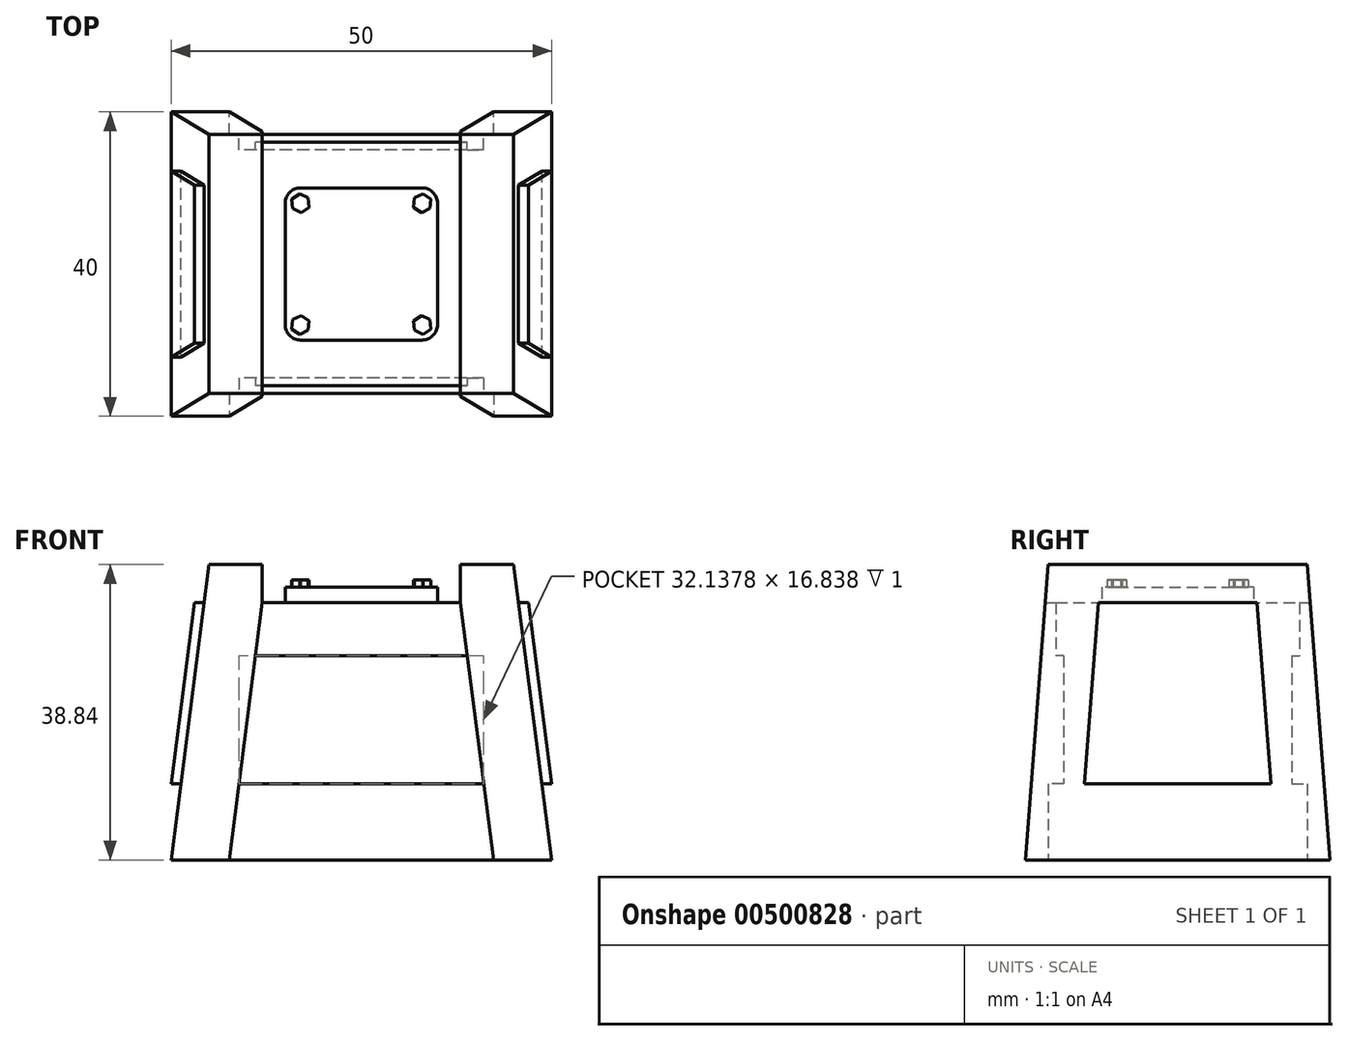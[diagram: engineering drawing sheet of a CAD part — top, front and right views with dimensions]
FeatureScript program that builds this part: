
annotation { "Feature Type Name" : "Feature", "Feature Type Description" : "" }
export const myFeature = defineFeature(function(context is Context, id is Id, definition is map)
    precondition{}
    {
        {
            var Q0;
            Q0=qCreatedBy(makeId("Front.planeOp"),FACE);
            var sketch = newSketch(context, id + "F0", { "sketchPlane" : qUnion([Q0])});
            skLineSegment(sketch, "E0", {"start": v(-25, 0) * mm, "end": v(25, 0) * mm});
            skPoint(sketch, "E1", {"position": v(0, 0) * mm});
            skLineSegment(sketch, "E2", {"start": v(-25, 0) * mm, "end": v(-20, 38.84) * mm});
            skLineSegment(sketch, "E3", {"start": v(-13, 38.84) * mm, "end": v(-13, 33.84) * mm});
            skLineSegment(sketch, "E4", {"start": v(-13, 33.84) * mm, "end": v(0, 33.84) * mm});
            skLineSegment(sketch, "E5", {"start": v(-13, 33.84) * mm, "end": v(-17.36, 0) * mm});
            skLineSegment(sketch, "E6", {"start": v(0, 10) * mm, "end": v(-16.07, 10) * mm});
            skLineSegment(sketch, "E7", {"start": v(0, 26.84) * mm, "end": v(-13.9, 26.84) * mm});
            skLineSegment(sketch, "E8", {"start": v(0, 0) * mm, "end": v(0, 10) * mm, "construction": true});
            skLineSegment(sketch, "E9", {"start": v(0, 0) * mm, "end": v(0, 38.84) * mm, "construction": true});
            skLineSegment(sketch, "E10", {"start": v(0, 38.84) * mm, "end": v(0, 33.84) * mm, "construction": true});
            skLineSegment(sketch, "E11", {"start": v(0, 33.84) * mm, "end": v(0, 26.84) * mm, "construction": true});
            skLineSegment(sketch, "E12", {"start": v(-20, 38.84) * mm, "end": v(-13, 38.84) * mm});
            skLineSegment(sketch, "E13.MirrorCS", {"start": v(0, 10) * mm, "end": v(16.07, 10) * mm});
            skLineSegment(sketch, "E14.MirrorCS", {"start": v(13, 33.84) * mm, "end": v(17.36, 0) * mm});
            skLineSegment(sketch, "E15.MirrorCS", {"start": v(0, 26.84) * mm, "end": v(13.9, 26.84) * mm});
            skLineSegment(sketch, "E16.MirrorCS", {"start": v(13, 33.84) * mm, "end": v(0, 33.84) * mm});
            skLineSegment(sketch, "E17.MirrorCS", {"start": v(13, 38.84) * mm, "end": v(13, 33.84) * mm});
            skLineSegment(sketch, "E18.MirrorCS", {"start": v(25, 0) * mm, "end": v(20, 38.84) * mm});
            skLineSegment(sketch, "E19.MirrorCS", {"start": v(20, 38.84) * mm, "end": v(13, 38.84) * mm});
            skLineSegment(sketch, "E20", {"start": v(0, 38.84) * mm, "end": v(-20, 38.84) * mm, "construction": true});
            skLineSegment(sketch, "E21", {"start": v(-25, 0) * mm, "end": v(-25, 38.84) * mm});
            skLineSegment(sketch, "E22", {"start": v(-25, 38.84) * mm, "end": v(-20, 38.84) * mm});
            skLineSegment(sketch, "E23.MirrorCS", {"start": v(25, 0) * mm, "end": v(25, 38.84) * mm});
            skLineSegment(sketch, "E24.MirrorCS", {"start": v(25, 38.84) * mm, "end": v(20, 38.84) * mm});
            skLineSegment(sketch, "E25", {"start": v(16.07, 10) * mm, "end": v(25, 10) * mm, "construction": true});
            skLineSegment(sketch, "E26", {"start": v(25, 10) * mm, "end": v(21.29, 38.84) * mm});
            skLineSegment(sketch, "E27.MirrorCS", {"start": v(-25, 10) * mm, "end": v(-21.29, 38.84) * mm});
            skSolve(sketch);
        }
        {
            var Q0;
            {var subQ3=sQuery(id+"F0.wireOp",EDGE,"E2");Q0=makeQuery(id+"F0.imprint","IMPRINT",FACE,{"disambiguationData":[TD([[makeQuery(id+"F0.imprint","IMPRINT",EDGE,{"derivedFrom":subQ3}),-1.0]])]});}
            var Q1;
            {var subQ6=sQuery(id+"F0.wireOp",EDGE,"E6");Q1=makeQuery(id+"F0.imprint","IMPRINT",FACE,{"disambiguationData":[TD([[makeQuery(id+"F0.imprint","IMPRINT",EDGE,{"derivedFrom":subQ6}),1.0]])]});}
            var Q2;
            {var subQ1=sQuery(id+"F0.wireOp",EDGE,"E6");Q2=makeQuery(id+"F0.imprint","IMPRINT",FACE,{"disambiguationData":[TD([[makeQuery(id+"F0.imprint","IMPRINT",EDGE,{"derivedFrom":subQ1}),-1.0]])]});}
            var Q3;
            {var subQ4=sQuery(id+"F0.wireOp",EDGE,"E4");Q3=makeQuery(id+"F0.imprint","IMPRINT",FACE,{"disambiguationData":[TD([[makeQuery(id+"F0.imprint","IMPRINT",EDGE,{"derivedFrom":subQ4}),-1.0]])]});}
            var Q4;
            {var subQ5=sQuery(id+"F0.wireOp",EDGE,"E17.MirrorCS");Q4=makeQuery(id+"F0.imprint","IMPRINT",FACE,{"disambiguationData":[TD([[makeQuery(id+"F0.imprint","IMPRINT",EDGE,{"derivedFrom":subQ5}),1.0]])]});}
            extrude(context, id + "F1", {"entities" : qUnion([Q0, Q1, Q2, Q3, Q4]), "depth" : 40 * mm});
        }
        {
            var Q0;
            {var subQ4=sQuery(id+"F0.wireOp",EDGE,"E4");Q0=makeQuery(id+"F0.imprint","IMPRINT",FACE,{"disambiguationData":[TD([[makeQuery(id+"F0.imprint","IMPRINT",EDGE,{"derivedFrom":subQ4}),-1.0]])]});}
            extrude(context, id + "F2", {"entities" : qUnion([Q0]), "operationType" : NewBodyOperationType.REMOVE, "depth" : 4 * mm});
        }
        {
            var Q0;
            {var subQ6=sQuery(id+"F0.wireOp",EDGE,"E6");Q0=makeQuery(id+"F0.imprint","IMPRINT",FACE,{"disambiguationData":[TD([[makeQuery(id+"F0.imprint","IMPRINT",EDGE,{"derivedFrom":subQ6}),1.0]])]});}
            extrude(context, id + "F3", {"entities" : qUnion([Q0]), "operationType" : NewBodyOperationType.REMOVE, "depth" : 3 * mm});
        }
        {
            var Q0;
            {var subQ1=sQuery(id+"F0.wireOp",EDGE,"E6");Q0=makeQuery(id+"F0.imprint","IMPRINT",FACE,{"disambiguationData":[TD([[makeQuery(id+"F0.imprint","IMPRINT",EDGE,{"derivedFrom":subQ1}),-1.0]])]});}
            extrude(context, id + "F4", {"entities" : qUnion([Q0]), "operationType" : NewBodyOperationType.REMOVE, "depth" : 5 * mm});
        }
        {
            var Q0;
            Q0=makeQuery(id+"F1.opExtrude","CAP_FACE",FACE,{"disambiguationData":[OSD([sQuery(id+"F0.wireOp",EDGE,"E0"),sQuery(id+"F0.wireOp",EDGE,"E2"),sQuery(id+"F0.wireOp",EDGE,"E3"),sQuery(id+"F0.wireOp",EDGE,"E4"),sQuery(id+"F0.wireOp",EDGE,"E12"),sQuery(id+"F0.wireOp",EDGE,"E16.MirrorCS"),sQuery(id+"F0.wireOp",EDGE,"E17.MirrorCS"),sQuery(id+"F0.wireOp",EDGE,"E18.MirrorCS"),sQuery(id+"F0.wireOp",EDGE,"E19.MirrorCS")])],"isStart":false});
            var sketch = newSketch(context, id + "F5", { "sketchPlane" : qUnion([Q0])});
            skLineSegment(sketch, "E28", {"start": v(-25, 0) * mm, "end": v(25, 0) * mm});
            skPoint(sketch, "E29", {"position": v(0, 0) * mm});
            skLineSegment(sketch, "E30", {"start": v(-25, 0) * mm, "end": v(-20, 38.84) * mm});
            skLineSegment(sketch, "E31", {"start": v(-13, 38.84) * mm, "end": v(-13, 33.84) * mm});
            skLineSegment(sketch, "E32", {"start": v(-13, 33.84) * mm, "end": v(0, 33.84) * mm});
            skLineSegment(sketch, "E33", {"start": v(-13, 33.84) * mm, "end": v(-17.36, 0) * mm});
            skLineSegment(sketch, "E34", {"start": v(0, 10) * mm, "end": v(-16.07, 10) * mm});
            skLineSegment(sketch, "E35", {"start": v(0, 26.84) * mm, "end": v(-13.9, 26.84) * mm});
            skLineSegment(sketch, "E36", {"start": v(0, 0) * mm, "end": v(0, 10) * mm, "construction": true});
            skLineSegment(sketch, "E37", {"start": v(0, 0) * mm, "end": v(0, 38.84) * mm, "construction": true});
            skLineSegment(sketch, "E38", {"start": v(0, 38.84) * mm, "end": v(0, 33.84) * mm, "construction": true});
            skLineSegment(sketch, "E39", {"start": v(0, 33.84) * mm, "end": v(0, 26.84) * mm, "construction": true});
            skLineSegment(sketch, "E40", {"start": v(-20, 38.84) * mm, "end": v(-13, 38.84) * mm});
            skLineSegment(sketch, "E41.MirrorCS", {"start": v(0, 10) * mm, "end": v(16.07, 10) * mm});
            skLineSegment(sketch, "E42.MirrorCS", {"start": v(13, 33.84) * mm, "end": v(17.36, 0) * mm});
            skLineSegment(sketch, "E43.MirrorCS", {"start": v(0, 26.84) * mm, "end": v(13.9, 26.84) * mm});
            skLineSegment(sketch, "E44.MirrorCS", {"start": v(13, 33.84) * mm, "end": v(0, 33.84) * mm});
            skLineSegment(sketch, "E45.MirrorCS", {"start": v(13, 38.84) * mm, "end": v(13, 33.84) * mm});
            skLineSegment(sketch, "E46.MirrorCS", {"start": v(25, 0) * mm, "end": v(20, 38.84) * mm});
            skLineSegment(sketch, "E47.MirrorCS", {"start": v(20, 38.84) * mm, "end": v(13, 38.84) * mm});
            skLineSegment(sketch, "E48", {"start": v(0, 38.84) * mm, "end": v(-20, 38.84) * mm, "construction": true});
            skSolve(sketch);
        }
        {
            var Q0;
            {var subQ4=sQuery(id+"F5.wireOp",EDGE,"E32");Q0=makeQuery(id+"F5.imprint","IMPRINT",FACE,{"disambiguationData":[TD([[makeQuery(id+"F5.imprint","IMPRINT",EDGE,{"derivedFrom":subQ4}),-1.0]])]});}
            extrude(context, id + "F6", {"entities" : qUnion([Q0]), "operationType" : NewBodyOperationType.REMOVE, "oppositeDirection" : true, "depth" : 4 * mm});
        }
        {
            var Q0;
            {var subQ6=sQuery(id+"F5.wireOp",EDGE,"E34");Q0=makeQuery(id+"F5.imprint","IMPRINT",FACE,{"disambiguationData":[TD([[makeQuery(id+"F5.imprint","IMPRINT",EDGE,{"derivedFrom":subQ6}),1.0]])]});}
            extrude(context, id + "F7", {"entities" : qUnion([Q0]), "operationType" : NewBodyOperationType.REMOVE, "oppositeDirection" : true, "depth" : 3 * mm});
        }
        {
            var Q0;
            {var subQ1=sQuery(id+"F5.wireOp",EDGE,"E34");Q0=makeQuery(id+"F5.imprint","IMPRINT",FACE,{"disambiguationData":[TD([[makeQuery(id+"F5.imprint","IMPRINT",EDGE,{"derivedFrom":subQ1}),-1.0]])]});}
            extrude(context, id + "F8", {"entities" : qUnion([Q0]), "operationType" : NewBodyOperationType.REMOVE, "oppositeDirection" : true, "depth" : 5 * mm});
        }
        {
            var Q0;
            Q0=makeQuery(id+"F1.opExtrude","SWEPT_FACE",FACE,{"disambiguationData":[OSD([sQuery(id+"F0.wireOp",EDGE,"E4"),sQuery(id+"F0.wireOp",EDGE,"E16.MirrorCS")])]});
            var sketch = newSketch(context, id + "F9", { "sketchPlane" : qUnion([Q0])});
            skLineSegment(sketch, "E49", {"start": v(0, -4) * mm, "end": v(0, -36) * mm, "construction": true});
            skLineSegment(sketch, "E50", {"start": v(0, -20) * mm, "end": v(-13, -20) * mm, "construction": true});
            skLineSegment(sketch, "E51.bottom", {"start": v(-8, -30) * mm, "end": v(8, -30) * mm});
            skLineSegment(sketch, "E51.top", {"start": v(-8, -10) * mm, "end": v(8, -10) * mm});
            skLineSegment(sketch, "E51.left", {"start": v(-10, -28) * mm, "end": v(-10, -12) * mm});
            skLineSegment(sketch, "E51.right", {"start": v(10, -28) * mm, "end": v(10, -12) * mm});
            skLineSegment(sketch, "E52", {"start": v(0, -10) * mm, "end": v(0, -30) * mm, "construction": true});
            skLineSegment(sketch, "E53", {"start": v(-10, -20) * mm, "end": v(10, -20) * mm, "construction": true});
            skPoint(sketch, "E54", {"position": v(0, -20) * mm});
            skPoint(sketch, "E55.visualSharp", {"position": v(-10, -30) * mm});
            skArc(sketch, "E55.filletArc", {"start": v(-10, -28) * mm, "mid": v(-9.41, -29.41) * mm, "end": v(-8, -30) * mm});
            skPoint(sketch, "E56.visualSharp", {"position": v(-10, -10) * mm});
            skArc(sketch, "E56.filletArc", {"start": v(-8, -10) * mm, "mid": v(-9.41, -10.59) * mm, "end": v(-10, -12) * mm});
            skPoint(sketch, "E57.visualSharp", {"position": v(10, -10) * mm});
            skArc(sketch, "E57.filletArc", {"start": v(10, -12) * mm, "mid": v(9.41, -10.59) * mm, "end": v(8, -10) * mm});
            skPoint(sketch, "E58.visualSharp", {"position": v(10, -30) * mm});
            skArc(sketch, "E58.filletArc", {"start": v(8, -30) * mm, "mid": v(9.41, -29.41) * mm, "end": v(10, -28) * mm});
            skSolve(sketch);
        }
        {
            var Q0;
            Q0=makeQuery(id+"F9.imprint","IMPRINT",FACE,{"disambiguationData":[TD([[makeQuery(id+"F9.imprint","IMPRINT",EDGE,{"derivedFrom":sQuery(id+"F9.wireOp",EDGE,"E51.bottom")}),1.0]])]});
            extrude(context, id + "F10", {"entities" : qUnion([Q0]), "operationType" : NewBodyOperationType.ADD, "depth" : 2 * mm});
        }
        {
            var Q0;
            Q0=makeQuery(id+"F0.imprint","IMPRINT",FACE,{"disambiguationData":[TD([[makeQuery(id+"F0.imprint","IMPRINT",EDGE,{"derivedFrom":sQuery(id+"F0.wireOp",EDGE,"E2")}),1.0]])]});
            var Q1;
            Q1=sQuery(id+"F0.wireOp",EDGE,"E21");
            extrude(context, id + "F11", {"entities" : qUnion([Q0]), "bodyType" : ToolBodyType.SURFACE, "surfaceEntities" : qUnion([Q1]), "depth" : 40 * mm});
        }
        {
            var Q0;
            Q0=makeQuery(id+"F11.opExtrude","SWEPT_FACE",FACE,{"disambiguationData":[OSD([sQuery(id+"F0.wireOp",EDGE,"E21")])]});
            var sketch = newSketch(context, id + "F12", { "sketchPlane" : qUnion([Q0])});
            skLineSegment(sketch, "E59", {"start": v(0, 0) * mm, "end": v(-3, 38.84) * mm});
            skLineSegment(sketch, "E60", {"start": v(-3, 38.84) * mm, "end": v(0, 38.84) * mm, "construction": true});
            skLineSegment(sketch, "E61", {"start": v(-20, 0) * mm, "end": v(-20, 38.84) * mm, "construction": true});
            skLineSegment(sketch, "E62.MirrorCS", {"start": v(-40, 0) * mm, "end": v(-37, 38.84) * mm});
            skLineSegment(sketch, "E63", {"start": v(-40, 0) * mm, "end": v(-40, 10) * mm, "construction": true});
            skLineSegment(sketch, "E64", {"start": v(-40, 38.84) * mm, "end": v(-40, 33.84) * mm, "construction": true});
            skLineSegment(sketch, "E65", {"start": v(-37.39, 33.84) * mm, "end": v(-30.39, 33.84) * mm, "construction": true});
            skLineSegment(sketch, "E66", {"start": v(-30.39, 33.84) * mm, "end": v(-32.23, 10) * mm});
            skLineSegment(sketch, "E67", {"start": v(-32.23, 10) * mm, "end": v(-20, 10) * mm});
            skLineSegment(sketch, "E68", {"start": v(-30.39, 33.84) * mm, "end": v(-20, 33.84) * mm});
            skLineSegment(sketch, "E69.MirrorCS", {"start": v(-9.61, 33.84) * mm, "end": v(-20, 33.84) * mm});
            skLineSegment(sketch, "E70.MirrorCS", {"start": v(-9.61, 33.84) * mm, "end": v(-7.77, 10) * mm});
            skLineSegment(sketch, "E71.MirrorCS", {"start": v(-7.77, 10) * mm, "end": v(-20, 10) * mm});
            skSolve(sketch);
        }
        {
            var Q0;
            {var subQ0=sQuery(id+"F12.wireOp",EDGE,"E59");Q0=makeQuery(id+"F12.imprint","IMPRINT",FACE,{"disambiguationData":[TD([[makeQuery(id+"F12.imprint","IMPRINT",EDGE,{"derivedFrom":subQ0}),-1.0]])]});}
            var Q1;
            {var subQ0=sQuery(id+"F12.wireOp",EDGE,"E62.MirrorCS");Q1=makeQuery(id+"F12.imprint","IMPRINT",FACE,{"disambiguationData":[TD([[makeQuery(id+"F12.imprint","IMPRINT",EDGE,{"derivedFrom":subQ0}),1.0]])]});}
            extrude(context, id + "F13", {"entities" : qUnion([Q0, Q1]), "operationType" : NewBodyOperationType.REMOVE, "depth" : 50 * mm});
        }
        {
            var Q0;
            Q0=makeQuery(id+"F10.opExtrude","CAP_FACE",FACE,{"disambiguationData":[OSD([sQuery(id+"F9.wireOp",EDGE,"E51.bottom"),sQuery(id+"F9.wireOp",EDGE,"E51.top"),sQuery(id+"F9.wireOp",EDGE,"E51.left"),sQuery(id+"F9.wireOp",EDGE,"E51.right"),sQuery(id+"F9.wireOp",EDGE,"E55.filletArc"),sQuery(id+"F9.wireOp",EDGE,"E56.filletArc"),sQuery(id+"F9.wireOp",EDGE,"E57.filletArc"),sQuery(id+"F9.wireOp",EDGE,"E58.filletArc")])],"isStart":false});
            var sketch = newSketch(context, id + "F14", { "sketchPlane" : qUnion([Q0])});
            skLineSegment(sketch, "E72", {"start": v(-10, -12) * mm, "end": v(-8, -12) * mm, "construction": true});
            skLineSegment(sketch, "E73", {"start": v(-8, -12) * mm, "end": v(-8, -10) * mm, "construction": true});
            skCircle(sketch, "E74.cCircle", {"center": v(-8, -12) * mm, "radius": 1.25 * mm, "construction": true});
            skLineSegment(sketch, "E74.0", {"start": v(-6.87, -12.54) * mm, "end": v(-7.9, -13.25) * mm});
            skLineSegment(sketch, "E74.1", {"start": v(-7.9, -13.25) * mm, "end": v(-9.03, -12.7) * mm});
            skLineSegment(sketch, "E74.2", {"start": v(-9.03, -12.7) * mm, "end": v(-9.13, -11.46) * mm});
            skLineSegment(sketch, "E74.3", {"start": v(-9.13, -11.46) * mm, "end": v(-8.1, -10.75) * mm});
            skLineSegment(sketch, "E74.4", {"start": v(-8.1, -10.75) * mm, "end": v(-6.97, -11.3) * mm});
            skLineSegment(sketch, "E74.5", {"start": v(-6.97, -11.3) * mm, "end": v(-6.87, -12.54) * mm});
            skLineSegment(sketch, "E75", {"start": v(0, -10) * mm, "end": v(0, -30) * mm, "construction": true});
            skLineSegment(sketch, "E76", {"start": v(-10, -20) * mm, "end": v(10, -20) * mm, "construction": true});
            skCircle(sketch, "E77.MirrorC", {"center": v(-8, -28) * mm, "radius": 1.25 * mm, "construction": true});
            skLineSegment(sketch, "E78.MirrorCS", {"start": v(-6.87, -27.46) * mm, "end": v(-7.9, -26.75) * mm});
            skLineSegment(sketch, "E79.MirrorCS", {"start": v(-6.97, -28.7) * mm, "end": v(-6.87, -27.46) * mm});
            skLineSegment(sketch, "E80.MirrorCS", {"start": v(-8.1, -29.25) * mm, "end": v(-6.97, -28.7) * mm});
            skLineSegment(sketch, "E81.MirrorCS", {"start": v(-9.13, -28.54) * mm, "end": v(-8.1, -29.25) * mm});
            skLineSegment(sketch, "E82.MirrorCS", {"start": v(-10, -28) * mm, "end": v(-8, -28) * mm, "construction": true});
            skLineSegment(sketch, "E83.MirrorCS", {"start": v(-9.03, -27.3) * mm, "end": v(-9.13, -28.54) * mm});
            skLineSegment(sketch, "E84.MirrorCS", {"start": v(-7.9, -26.75) * mm, "end": v(-9.03, -27.3) * mm});
            skLineSegment(sketch, "E85.MirrorCS", {"start": v(6.87, -27.46) * mm, "end": v(7.9, -26.75) * mm});
            skLineSegment(sketch, "E86.MirrorCS", {"start": v(6.97, -28.7) * mm, "end": v(6.87, -27.46) * mm});
            skLineSegment(sketch, "E87.MirrorCS", {"start": v(8.1, -29.25) * mm, "end": v(6.97, -28.7) * mm});
            skLineSegment(sketch, "E88.MirrorCS", {"start": v(9.13, -28.54) * mm, "end": v(8.1, -29.25) * mm});
            skLineSegment(sketch, "E89.MirrorCS", {"start": v(10, -28) * mm, "end": v(8, -28) * mm, "construction": true});
            skLineSegment(sketch, "E90.MirrorCS", {"start": v(9.03, -27.3) * mm, "end": v(9.13, -28.54) * mm});
            skLineSegment(sketch, "E91.MirrorCS", {"start": v(7.9, -26.75) * mm, "end": v(9.03, -27.3) * mm});
            skLineSegment(sketch, "E92.MirrorCS", {"start": v(6.87, -12.54) * mm, "end": v(7.9, -13.25) * mm});
            skLineSegment(sketch, "E93.MirrorCS", {"start": v(6.97, -11.3) * mm, "end": v(6.87, -12.54) * mm});
            skLineSegment(sketch, "E94.MirrorCS", {"start": v(8.1, -10.75) * mm, "end": v(6.97, -11.3) * mm});
            skLineSegment(sketch, "E95.MirrorCS", {"start": v(9.13, -11.46) * mm, "end": v(8.1, -10.75) * mm});
            skLineSegment(sketch, "E96.MirrorCS", {"start": v(9.03, -12.7) * mm, "end": v(9.13, -11.46) * mm});
            skLineSegment(sketch, "E97.MirrorCS", {"start": v(7.9, -13.25) * mm, "end": v(9.03, -12.7) * mm});
            skCircle(sketch, "E98.MirrorC", {"center": v(8, -12) * mm, "radius": 1.25 * mm, "construction": true});
            skSolve(sketch);
        }
        {
            var Q0;
            Q0=makeQuery(id+"F14.imprint","IMPRINT",FACE,{"disambiguationData":[TD([[makeQuery(id+"F14.imprint","IMPRINT",EDGE,{"derivedFrom":sQuery(id+"F14.wireOp",EDGE,"E74.0")}),-1.0]])]});
            var Q1;
            Q1=makeQuery(id+"F14.imprint","IMPRINT",FACE,{"disambiguationData":[TD([[makeQuery(id+"F14.imprint","IMPRINT",EDGE,{"derivedFrom":sQuery(id+"F14.wireOp",EDGE,"E93.MirrorCS")}),1.0]])]});
            var Q2;
            Q2=makeQuery(id+"F14.imprint","IMPRINT",FACE,{"disambiguationData":[TD([[makeQuery(id+"F14.imprint","IMPRINT",EDGE,{"derivedFrom":sQuery(id+"F14.wireOp",EDGE,"E85.MirrorCS")}),-1.0]])]});
            var Q3;
            Q3=makeQuery(id+"F14.imprint","IMPRINT",FACE,{"disambiguationData":[TD([[makeQuery(id+"F14.imprint","IMPRINT",EDGE,{"derivedFrom":sQuery(id+"F14.wireOp",EDGE,"E78.MirrorCS")}),1.0]])]});
            extrude(context, id + "F15", {"entities" : qUnion([Q0, Q1, Q2, Q3]), "operationType" : NewBodyOperationType.ADD, "depth" : 1 * mm});
        }
        {
            var Q0;
            Q0=makeQuery(id+"F12.imprint","IMPRINT",FACE,{"disambiguationData":[TD([[makeQuery(id+"F12.imprint","IMPRINT",EDGE,{"derivedFrom":sQuery(id+"F12.wireOp",EDGE,"E66")}),1.0]])]});
            extrude(context, id + "F16", {"entities" : qUnion([Q0]), "operationType" : NewBodyOperationType.ADD, "depth" : 50 * mm});
        }
        {
            var Q0;
            {var subQ0=sQuery(id+"F0.wireOp",EDGE,"E22");var subQ1=sQuery(id+"F0.wireOp",EDGE,"E21");var subQ2=makeQuery(id+"F0.imprint","INTERSECT",VERTEX,{"derivedFrom":[subQ1,subQ0]});Q0=makeQuery(id+"F0.imprint","IMPRINT",FACE,{"disambiguationData":[TD([[makeQuery(id+"F0.imprint","IMPRINT",EDGE,{"disambiguationData":[TD([[subQ2,1.0]])],"derivedFrom":subQ1}),-1.0]])]});}
            var Q1;
            {var subQ0=sQuery(id+"F0.wireOp",EDGE,"E24.MirrorCS");var subQ1=sQuery(id+"F0.wireOp",EDGE,"E23.MirrorCS");var subQ2=makeQuery(id+"F0.imprint","INTERSECT",VERTEX,{"derivedFrom":[subQ1,subQ0]});Q1=makeQuery(id+"F0.imprint","IMPRINT",FACE,{"disambiguationData":[TD([[makeQuery(id+"F0.imprint","IMPRINT",EDGE,{"disambiguationData":[TD([[subQ2,1.0]])],"derivedFrom":subQ1}),1.0]])]});}
            extrude(context, id + "F17", {"entities" : qUnion([Q0, Q1]), "operationType" : NewBodyOperationType.REMOVE, "depth" : 40 * mm});
        }
    });
